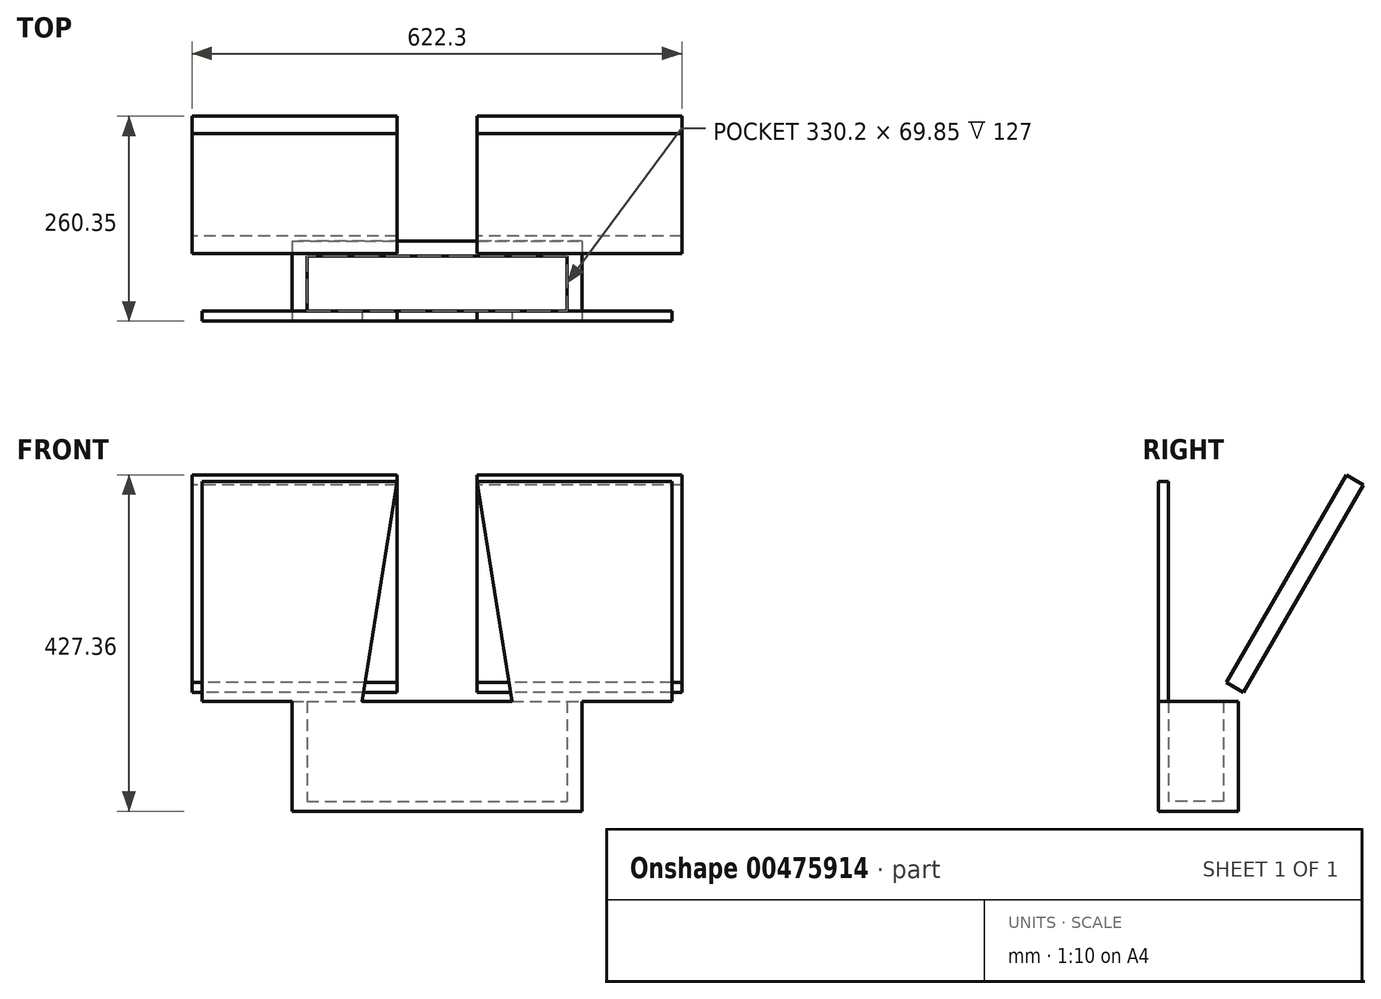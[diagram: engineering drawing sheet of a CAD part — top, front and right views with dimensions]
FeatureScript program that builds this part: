
annotation { "Feature Type Name" : "Feature", "Feature Type Description" : "" }
export const myFeature = defineFeature(function(context is Context, id is Id, definition is map)
    precondition{}
    {
        {
            var Q0;
            Q0=qCreatedBy(makeId("Top.planeOp"),FACE);
            var sketch = newSketch(context, id + "F0", { "sketchPlane" : qUnion([Q0])});
            skLineSegment(sketch, "E0.bottom", {"start": v(165.1, 50.8) * mm, "end": v(-165.1, 50.8) * mm});
            skLineSegment(sketch, "E0.top", {"start": v(165.1, -50.8) * mm, "end": v(-165.1, -50.8) * mm});
            skLineSegment(sketch, "E0.left", {"start": v(165.1, 50.8) * mm, "end": v(165.1, -50.8) * mm});
            skLineSegment(sketch, "E0.right", {"start": v(-165.1, 50.8) * mm, "end": v(-165.1, -50.8) * mm});
            skPoint(sketch, "E0.middle", {"position": v(0, 0) * mm});
            skSolve(sketch);
        }
        {
            var Q0;
            Q0 = qSketchRegion(id + "F0", true);
            extrude(context, id + "F1", {"entities" : qUnion([Q0]), "endBound" : BoundingType.SYMMETRIC, "depth" : 12.7 * mm, "offsetDistance" : 25.4 * mm});
        }
        {
            var Q0;
            Q0=makeQuery(id+"F1.opExtrude","SWEPT_FACE",FACE,{"disambiguationData":[OSD([sQuery(id+"F0.wireOp",EDGE,"E0.right")])]});
            var sketch = newSketch(context, id + "F2", { "sketchPlane" : qUnion([Q0])});
            skLineSegment(sketch, "E1.bottom", {"start": v(-50.8, -6.35) * mm, "end": v(50.8, -6.35) * mm});
            skLineSegment(sketch, "E1.top", {"start": v(-50.8, 133.35) * mm, "end": v(50.8, 133.35) * mm});
            skLineSegment(sketch, "E1.left", {"start": v(-50.8, -6.35) * mm, "end": v(-50.8, 133.35) * mm});
            skLineSegment(sketch, "E1.right", {"start": v(50.8, -6.35) * mm, "end": v(50.8, 133.35) * mm});
            skSolve(sketch);
        }
        {
            var Q0;
            Q0 = qSketchRegion(id + "F2", true);
            extrude(context, id + "F3", {"entities" : qUnion([Q0]), "operationType" : NewBodyOperationType.ADD, "depth" : 19.05 * mm, "offsetDistance" : 25.4 * mm});
        }
        {
            var Q0;
            Q0=makeQuery(id+"F1.opExtrude","SWEPT_BODY",BODY,{"disambiguationData":[OSD([sQuery(id+"F0.wireOp",EDGE,"E0.bottom"),sQuery(id+"F0.wireOp",EDGE,"E0.top"),sQuery(id+"F0.wireOp",EDGE,"E0.left"),sQuery(id+"F0.wireOp",EDGE,"E0.right")])]});
            var Q1;
            Q1=qCreatedBy(makeId("Right.planeOp"),FACE);
            mirror(context, id + "F4", {"operationType" : NewBodyOperationType.ADD, "entities" : qUnion([Q0]), "mirrorPlane" : qUnion([Q1])});
        }
        {
            var Q0;
            Q0=makeQuery(id+"F1.opExtrude","CAP_FACE",FACE,{"disambiguationData":[OSD([sQuery(id+"F0.wireOp",EDGE,"E0.bottom"),sQuery(id+"F0.wireOp",EDGE,"E0.top"),sQuery(id+"F0.wireOp",EDGE,"E0.left"),sQuery(id+"F0.wireOp",EDGE,"E0.right")])],"isStart":false});
            var sketch = newSketch(context, id + "F5", { "sketchPlane" : qUnion([Q0])});
            skSolve(sketch);
        }
        {
            var Q0;
            Q0=makeQuery(id+"F5.imprint","IMPRINT",FACE,{"disambiguationData":[TD([[makeQuery(id+"F5.imprint","IMPRINT",EDGE,{"derivedFrom":makeQuery(id+"F1.opExtrude","CAP_EDGE",EDGE,{"disambiguationData":[OSD([sQuery(id+"F0.wireOp",EDGE,"E0.bottom")])],"isStart":false})}),1.0]])]});
            var sketch = newSketch(context, id + "F6", { "sketchPlane" : qUnion([Q0])});
            skLineSegment(sketch, "E2.bottom", {"start": v(-165.1, -38.1) * mm, "end": v(165.1, -38.1) * mm});
            skLineSegment(sketch, "E2.top", {"start": v(-165.1, -50.8) * mm, "end": v(165.1, -50.8) * mm});
            skLineSegment(sketch, "E2.left", {"start": v(-165.1, -38.1) * mm, "end": v(-165.1, -50.8) * mm});
            skLineSegment(sketch, "E2.right", {"start": v(165.1, -38.1) * mm, "end": v(165.1, -50.8) * mm});
            skSolve(sketch);
        }
        {
            var Q0;
            Q0 = qSketchRegion(id + "F6", true);
            extrude(context, id + "F7", {"entities" : qUnion([Q0]), "operationType" : NewBodyOperationType.ADD, "depth" : 127 * mm, "offsetDistance" : 25.4 * mm});
        }
        {
            var Q0;
            {var subQ0=makeQuery(id+"F3.boolean.opBoolean","MERGE",FACE,{"derivedFrom":[makeQuery(id+"F1.opExtrude","SWEPT_FACE",FACE,{"disambiguationData":[OSD([sQuery(id+"F0.wireOp",EDGE,"E0.top")])]}),makeQuery(id+"F3.opExtrude","SWEPT_FACE",FACE,{"disambiguationData":[OSD([sQuery(id+"F2.wireOp",EDGE,"E1.right")])]})]});Q0=makeQuery(id+"F7.boolean.opBoolean","MERGE",FACE,{"derivedFrom":[makeQuery(id+"F4.boolean.opBoolean","MERGE",FACE,{"derivedFrom":[subQ0,makeQuery(id+"F4.opPattern","COPY",FACE,{"derivedFrom":subQ0,"instanceName":"1"})]}),makeQuery(id+"F7.opExtrude","SWEPT_FACE",FACE,{"disambiguationData":[OSD([sQuery(id+"F6.wireOp",EDGE,"E2.top")])]})]});}
            var sketch = newSketch(context, id + "F8", { "sketchPlane" : qUnion([Q0])});
            skLineSegment(sketch, "E3.bottom", {"start": v(-298.45, 133.35) * mm, "end": v(298.45, 133.35) * mm});
            skLineSegment(sketch, "E3.top", {"start": v(-298.45, 412.75) * mm, "end": v(-95.25, 412.75) * mm});
            skLineSegment(sketch, "E3.left", {"start": v(-298.45, 133.35) * mm, "end": v(-298.45, 412.75) * mm});
            skLineSegment(sketch, "E3.right", {"start": v(298.45, 133.35) * mm, "end": v(298.45, 412.75) * mm});
            skLineSegment(sketch, "E4.trimOffspring", {"start": v(95.25, 412.75) * mm, "end": v(298.45, 412.75) * mm});
            skLineSegment(sketch, "E5", {"start": v(-95.25, 412.75) * mm, "end": v(-50.8, 412.75) * mm});
            skLineSegment(sketch, "E6.MirrorCS", {"start": v(95.25, 412.75) * mm, "end": v(50.8, 412.75) * mm});
            skLineSegment(sketch, "E7", {"start": v(-50.8, 412.75) * mm, "end": v(-95.25, 133.35) * mm});
            skLineSegment(sketch, "E8", {"start": v(50.8, 412.75) * mm, "end": v(95.25, 133.35) * mm});
            skSolve(sketch);
        }
        {
            var Q0;
            Q0 = qSketchRegion(id + "F8", true);
            extrude(context, id + "F9", {"entities" : qUnion([Q0]), "operationType" : NewBodyOperationType.ADD, "oppositeDirection" : true, "depth" : 12.7 * mm, "offsetDistance" : 25.4 * mm});
        }
        {
            var Q0;
            Q0=makeQuery(id+"F5.imprint","IMPRINT",FACE,{"disambiguationData":[TD([[makeQuery(id+"F5.imprint","IMPRINT",EDGE,{"derivedFrom":makeQuery(id+"F1.opExtrude","CAP_EDGE",EDGE,{"disambiguationData":[OSD([sQuery(id+"F0.wireOp",EDGE,"E0.bottom")])],"isStart":false})}),1.0]])]});
            var sketch = newSketch(context, id + "F10", { "sketchPlane" : qUnion([Q0])});
            skLineSegment(sketch, "E9.bottom", {"start": v(-165.1, 31.75) * mm, "end": v(165.1, 31.75) * mm});
            skLineSegment(sketch, "E9.top", {"start": v(-165.1, 50.8) * mm, "end": v(165.1, 50.8) * mm});
            skLineSegment(sketch, "E9.left", {"start": v(-165.1, 31.75) * mm, "end": v(-165.1, 50.8) * mm});
            skLineSegment(sketch, "E9.right", {"start": v(165.1, 31.75) * mm, "end": v(165.1, 50.8) * mm});
            skSolve(sketch);
        }
        {
            var Q0;
            Q0 = qSketchRegion(id + "F10", true);
            extrude(context, id + "F11", {"entities" : qUnion([Q0]), "operationType" : NewBodyOperationType.ADD, "depth" : 127 * mm, "offsetDistance" : 25.4 * mm});
        }
        {
            var Q0;
            {var subQ0=makeQuery(id+"F3.boolean.opBoolean","MERGE",FACE,{"derivedFrom":[makeQuery(id+"F1.opExtrude","SWEPT_FACE",FACE,{"disambiguationData":[OSD([sQuery(id+"F0.wireOp",EDGE,"E0.bottom")])]}),makeQuery(id+"F3.opExtrude","SWEPT_FACE",FACE,{"disambiguationData":[OSD([sQuery(id+"F2.wireOp",EDGE,"E1.left")])]})]});Q0=makeQuery(id+"F11.boolean.opBoolean","MERGE",FACE,{"derivedFrom":[makeQuery(id+"F4.boolean.opBoolean","MERGE",FACE,{"derivedFrom":[subQ0,makeQuery(id+"F4.opPattern","COPY",FACE,{"derivedFrom":subQ0,"instanceName":"1"})]}),makeQuery(id+"F11.opExtrude","SWEPT_FACE",FACE,{"disambiguationData":[OSD([sQuery(id+"F10.wireOp",EDGE,"E9.top")])]})]});}
            var sketch = newSketch(context, id + "F12", { "sketchPlane" : qUnion([Q0])});
            skLineSegment(sketch, "E10.bottom", {"start": v(-311.15, 450.85) * mm, "end": v(-50.8, 450.85) * mm});
            skLineSegment(sketch, "E10.top", {"start": v(-311.15, 146.05) * mm, "end": v(-50.8, 146.05) * mm});
            skLineSegment(sketch, "E10.left", {"start": v(-311.15, 450.85) * mm, "end": v(-311.15, 146.05) * mm});
            skLineSegment(sketch, "E10.right", {"start": v(311.15, 450.85) * mm, "end": v(311.15, 146.05) * mm});
            skLineSegment(sketch, "E11", {"start": v(-50.8, 450.85) * mm, "end": v(-50.8, 146.05) * mm});
            skLineSegment(sketch, "E12", {"start": v(50.8, 450.85) * mm, "end": v(50.8, 146.05) * mm});
            skLineSegment(sketch, "E13.trimOffspring", {"start": v(50.8, 450.85) * mm, "end": v(311.15, 450.85) * mm});
            skLineSegment(sketch, "E14.trimOffspring", {"start": v(50.8, 146.05) * mm, "end": v(311.15, 146.05) * mm});
            skSolve(sketch);
        }
        {
            var Q0;
            Q0 = qSketchRegion(id + "F12", true);
            extrude(context, id + "F13", {"entities" : qUnion([Q0]), "oppositeDirection" : true, "depth" : 25.4 * mm, "offsetDistance" : 25.4 * mm});
        }
        {
            var Q0;
            Q0=makeQuery(id+"F13.opExtrude","SWEPT_BODY",BODY,{"disambiguationData":[OSD([sQuery(id+"F12.wireOp",EDGE,"E10.bottom"),sQuery(id+"F12.wireOp",EDGE,"E10.top"),sQuery(id+"F12.wireOp",EDGE,"E10.left"),sQuery(id+"F12.wireOp",EDGE,"E11")])]});
            var Q1;
            Q1=makeQuery(id+"F13.opExtrude","SWEPT_BODY",BODY,{"disambiguationData":[OSD([sQuery(id+"F12.wireOp",EDGE,"E10.right"),sQuery(id+"F12.wireOp",EDGE,"E12"),sQuery(id+"F12.wireOp",EDGE,"E13.trimOffspring"),sQuery(id+"F12.wireOp",EDGE,"E14.trimOffspring")])]});
            var Q2;
            {var subQ0=makeQuery(id+"F3.opExtrude","SWEPT_EDGE",EDGE,{"disambiguationData":[OSD([sQuery(id+"F2.wireOp",EDGE,"E1.top"),sQuery(id+"F2.wireOp",EDGE,"E1.left")])]});Q2=makeQuery(id+"F11.boolean.opBoolean","MERGE",EDGE,{"derivedFrom":[subQ0,makeQuery(id+"F4.opPattern","COPY",EDGE,{"derivedFrom":subQ0,"instanceName":"1"}),makeQuery(id+"F11.opExtrude","CAP_EDGE",EDGE,{"disambiguationData":[OSD([sQuery(id+"F10.wireOp",EDGE,"E9.top")])],"isStart":false})]});}
            transform(context, id + "F14", {"entities" : qUnion([Q0, Q1]), "transformType" : TransformType.ROTATION, "transformAxis" : qUnion([Q2]), "angle" : 30 * degree, "oppositeDirection" : true, "makeCopy" : false});
        }
    });
